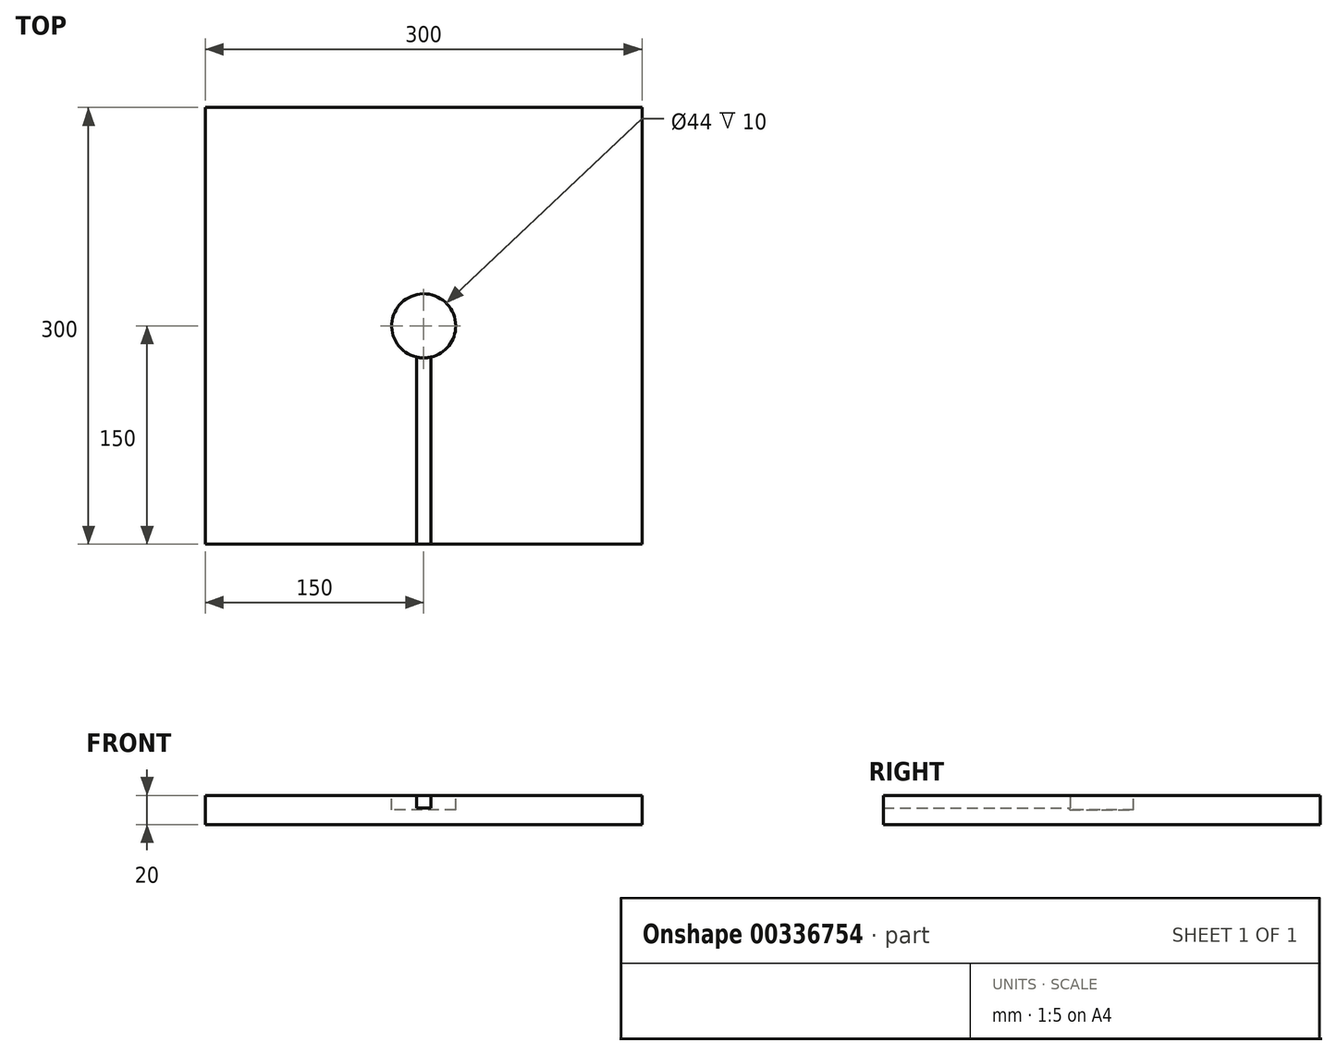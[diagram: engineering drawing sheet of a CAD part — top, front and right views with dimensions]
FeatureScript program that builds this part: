
annotation { "Feature Type Name" : "Feature", "Feature Type Description" : "" }
export const myFeature = defineFeature(function(context is Context, id is Id, definition is map)
    precondition{}
    {
        {
            var Q0;
            Q0=qCreatedBy(makeId("Top.planeOp"),FACE);
            var sketch = newSketch(context, id + "F0", { "sketchPlane" : qUnion([Q0])});
            skLineSegment(sketch, "E0.bottom", {"start": v(150, 150) * mm, "end": v(-150, 150) * mm});
            skLineSegment(sketch, "E0.top", {"start": v(150, -150) * mm, "end": v(-150, -150) * mm});
            skLineSegment(sketch, "E0.left", {"start": v(150, 150) * mm, "end": v(150, -150) * mm});
            skLineSegment(sketch, "E0.right", {"start": v(-150, 150) * mm, "end": v(-150, -150) * mm});
            skPoint(sketch, "E0.middle", {"position": v(0, 0) * mm});
            skSolve(sketch);
        }
        {
            var Q0;
            Q0 = qSketchRegion(id + "F0", true);
            extrude(context, id + "F1", {"entities" : qUnion([Q0]), "depth" : 20 * mm});
        }
        {
            var Q0;
            Q0=makeQuery(id+"F1.opExtrude","CAP_FACE",FACE,{"disambiguationData":[OSD([sQuery(id+"F0.wireOp",EDGE,"E0.bottom"),sQuery(id+"F0.wireOp",EDGE,"E0.top"),sQuery(id+"F0.wireOp",EDGE,"E0.left"),sQuery(id+"F0.wireOp",EDGE,"E0.right")])],"isStart":false});
            var sketch = newSketch(context, id + "F2", { "sketchPlane" : qUnion([Q0])});
            skLineSegment(sketch, "E1", {"start": v(-5, -150) * mm, "end": v(-5, -21.42) * mm});
            skLineSegment(sketch, "E2", {"start": v(5, -150) * mm, "end": v(5, -21.42) * mm});
            skArc(sketch, "E3", {"start": v(5, -21.42) * mm, "mid": v(0, 22) * mm, "end": v(-5, -21.42) * mm});
            skSolve(sketch);
        }
        {
            var Q0;
            {var subQ0=sQuery(id+"F2.wireOp",EDGE,"E3");var subQ1=makeQuery(id+"F2.imprint","INTERSECT",VERTEX,{"derivedFrom":[sQuery(id+"F2.wireOp",EDGE,"E1"),subQ0]});Q0=makeQuery(id+"F2.imprint","IMPRINT",FACE,{"disambiguationData":[TD([[makeQuery(id+"F2.imprint","IMPRINT",EDGE,{"disambiguationData":[TD([[subQ1,-1.0]])],"derivedFrom":subQ0}),1.0]])]});}
            var Q1;
            Q1=sQuery(id+"F2.wireOp",EDGE,"E3");
            extrude(context, id + "F3", {"entities" : qUnion([Q0]), "operationType" : NewBodyOperationType.REMOVE, "surfaceEntities" : qUnion([Q1]), "oppositeDirection" : true, "depth" : 10 * mm});
        }
        {
            var Q0;
            {var subQ0=sQuery(id+"F2.wireOp",EDGE,"E1");Q0=makeQuery(id+"F2.imprint","IMPRINT",FACE,{"disambiguationData":[TD([[makeQuery(id+"F2.imprint","IMPRINT",EDGE,{"derivedFrom":subQ0}),-1.0]])]});}
            extrude(context, id + "F4", {"entities" : qUnion([Q0]), "operationType" : NewBodyOperationType.REMOVE, "oppositeDirection" : true, "depth" : 8.8 * mm});
        }
        {
            var Q0;
            Q0=makeQuery(id+"F3.boolean.opBoolean","COPY",FACE,{"derivedFrom":makeQuery(id+"F3.opExtrude","CAP_FACE",FACE,{"disambiguationData":[OSD([sQuery(id+"F0.wireOp",EDGE,"E0.top"),sQuery(id+"F2.wireOp",EDGE,"E1"),sQuery(id+"F2.wireOp",EDGE,"E2"),sQuery(id+"F2.wireOp",EDGE,"E3")])],"isStart":false})});
            var sketch = newSketch(context, id + "F5", { "sketchPlane" : qUnion([Q0])});
            skArc(sketch, "E4", {"start": v(-5, -21.42) * mm, "mid": v(0, -22) * mm, "end": v(5, -21.42) * mm});
            skSolve(sketch);
        }
        {
            var Q0;
            Q0=makeQuery(id+"F5.imprint","IMPRINT",FACE,{"disambiguationData":[TD([[makeQuery(id+"F5.imprint","IMPRINT",EDGE,{"derivedFrom":sQuery(id+"F5.wireOp",EDGE,"E4")}),-1.0]])]});
            extrude(context, id + "F6", {"entities" : qUnion([Q0]), "operationType" : NewBodyOperationType.ADD, "depth" : 1.2 * mm});
        }
    });
